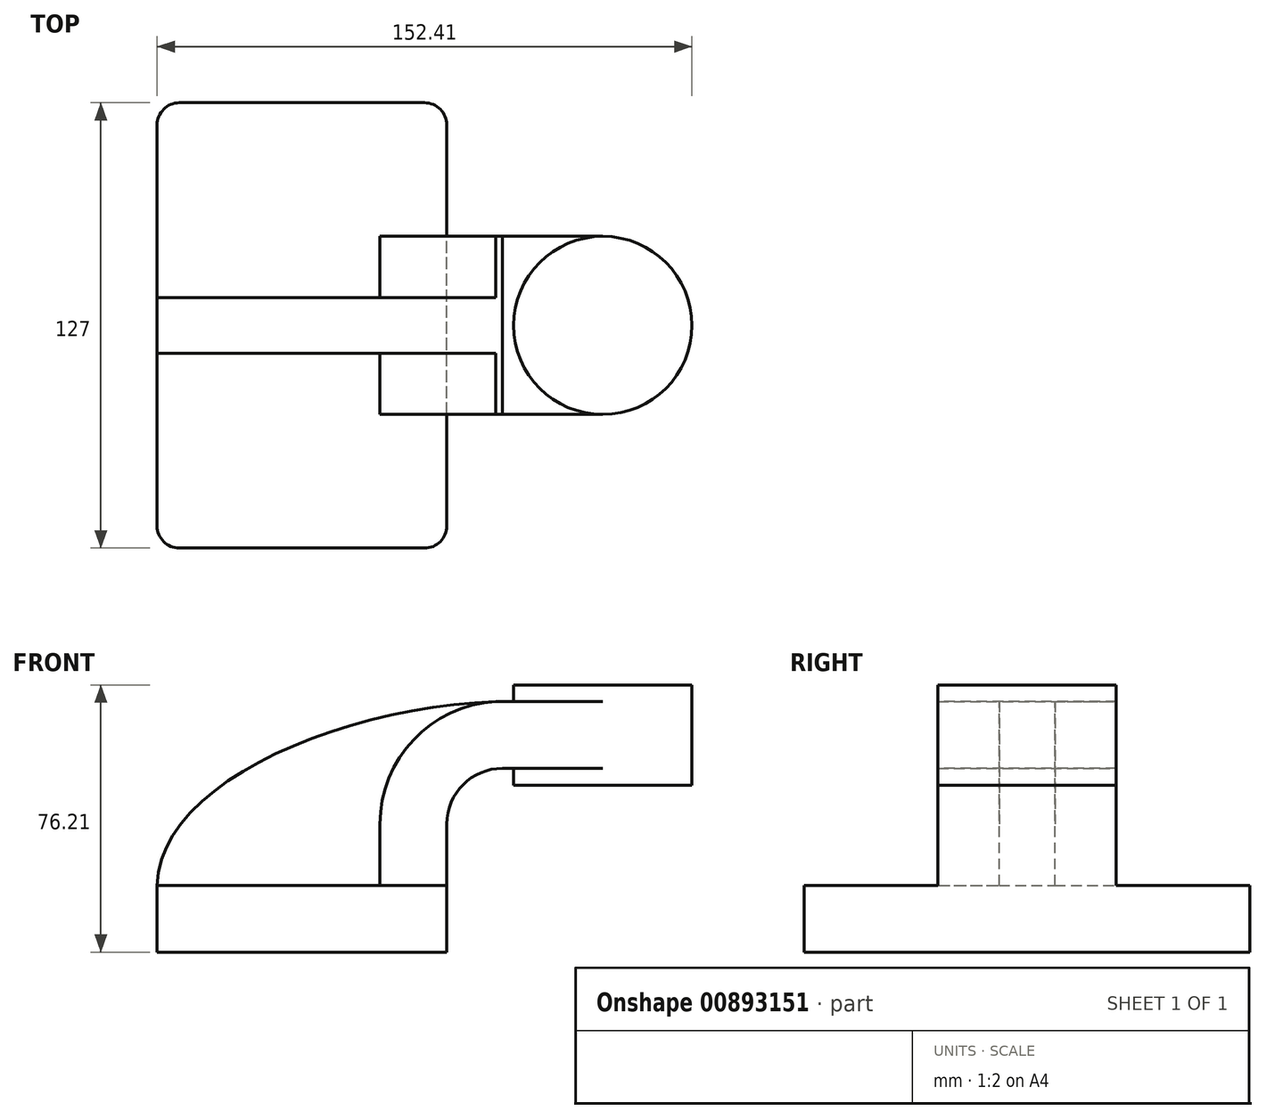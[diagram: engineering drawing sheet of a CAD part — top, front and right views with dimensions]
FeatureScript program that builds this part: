
annotation { "Feature Type Name" : "Feature", "Feature Type Description" : "" }
export const myFeature = defineFeature(function(context is Context, id is Id, definition is map)
    precondition{}
    {
        {
            var Q0;
            Q0=qCreatedBy(makeId("Front.planeOp"),FACE);
            var sketch = newSketch(context, id + "F0", { "sketchPlane" : qUnion([Q0])});
            skLineSegment(sketch, "E0.bottom", {"start": v(-41.28, 9.52) * mm, "end": v(41.27, 9.53) * mm});
            skLineSegment(sketch, "E0.top", {"start": v(-41.28, -9.53) * mm, "end": v(41.28, -9.53) * mm});
            skLineSegment(sketch, "E0.left", {"start": v(-41.28, 9.52) * mm, "end": v(-41.27, -9.53) * mm});
            skLineSegment(sketch, "E0.right", {"start": v(41.28, 9.53) * mm, "end": v(41.28, -9.52) * mm});
            skPoint(sketch, "E0.middle", {"position": v(0, 0) * mm});
            skLineSegment(sketch, "E1.bottom", {"start": v(111.12, 38.1) * mm, "end": v(60.32, 38.1) * mm});
            skLineSegment(sketch, "E1.top", {"start": v(111.12, 66.67) * mm, "end": v(60.32, 66.67) * mm});
            skLineSegment(sketch, "E1.left", {"start": v(111.12, 38.1) * mm, "end": v(111.12, 66.68) * mm});
            skLineSegment(sketch, "E1.right", {"start": v(60.32, 38.1) * mm, "end": v(60.32, 66.67) * mm});
            skPoint(sketch, "E1.middle", {"position": v(85.72, 52.39) * mm});
            skLineSegment(sketch, "E2", {"start": v(41.27, 9.53) * mm, "end": v(41.27, 27) * mm});
            skArc(sketch, "E3", {"start": v(57.15, 42.88) * mm, "mid": v(45.92, 38.23) * mm, "end": v(41.27, 27) * mm});
            skLineSegment(sketch, "E4", {"start": v(57.15, 42.88) * mm, "end": v(85.72, 42.88) * mm});
            skLineSegment(sketch, "E5.0", {"start": v(22.23, 9.53) * mm, "end": v(22.23, 27) * mm});
            skArc(sketch, "E5.1", {"start": v(57.15, 61.93) * mm, "mid": v(32.45, 51.7) * mm, "end": v(22.22, 27) * mm});
            skLineSegment(sketch, "E5.2", {"start": v(57.15, 61.93) * mm, "end": v(85.72, 61.93) * mm});
            skFitSpline(sketch, "E6", {"points": [v(-41.28, 9.52) * mm, v(57.15, 61.93) * mm], "startDerivative": vector(0.89, 86.65) * mm, "endDerivative": vector(137.6, 2.87) * mm});
            skLineSegment(sketch, "E7", {"start": v(85.72, 66.67) * mm, "end": v(85.72, 38.1) * mm});
            skSolve(sketch);
        }
        {
            var Q0;
            Q0=makeQuery(id+"F0.imprint","IMPRINT",FACE,{"disambiguationData":[TD([[makeQuery(id+"F0.imprint","IMPRINT",EDGE,{"derivedFrom":sQuery(id+"F0.wireOp",EDGE,"E0.top")}),1.0]])]});
            extrude(context, id + "F1", {"entities" : qUnion([Q0]), "endBound" : BoundingType.SYMMETRIC, "depth" : 127 * mm, "offsetDistance" : 25.4 * mm});
        }
        {
            var Q0;
            {var subQ1=sQuery(id+"F0.wireOp",EDGE,"E2");Q0=makeQuery(id+"F0.imprint","IMPRINT",FACE,{"disambiguationData":[TD([[makeQuery(id+"F0.imprint","IMPRINT",EDGE,{"derivedFrom":subQ1}),1.0]])]});}
            var Q1;
            {var subQ0=sQuery(id+"F0.wireOp",EDGE,"E4");var subQ1=sQuery(id+"F0.wireOp",EDGE,"E1.right");var subQ2=makeQuery(id+"F0.imprint","INTERSECT",VERTEX,{"derivedFrom":[subQ1,subQ0]});Q1=makeQuery(id+"F0.imprint","IMPRINT",FACE,{"disambiguationData":[TD([[makeQuery(id+"F0.imprint","IMPRINT",EDGE,{"disambiguationData":[TD([[subQ2,-1.0]])],"derivedFrom":subQ1}),-1.0]])]});}
            extrude(context, id + "F2", {"entities" : qUnion([Q0, Q1]), "operationType" : NewBodyOperationType.ADD, "endBound" : BoundingType.SYMMETRIC, "depth" : 50.8 * mm, "offsetDistance" : 25.4 * mm});
        }
        {
            var Q0;
            {var subQ3=sQuery(id+"F0.wireOp",EDGE,"E5.0");Q0=makeQuery(id+"F0.imprint","IMPRINT",FACE,{"disambiguationData":[TD([[makeQuery(id+"F0.imprint","IMPRINT",EDGE,{"derivedFrom":subQ3}),1.0]])]});}
            extrude(context, id + "F3", {"entities" : qUnion([Q0]), "operationType" : NewBodyOperationType.ADD, "endBound" : BoundingType.SYMMETRIC, "depth" : 15.88 * mm, "offsetDistance" : 25.4 * mm});
        }
        {
            var Q0;
            {var subQ4=sQuery(id+"F0.wireOp",EDGE,"E1.left");Q0=makeQuery(id+"F0.imprint","IMPRINT",FACE,{"disambiguationData":[TD([[makeQuery(id+"F0.imprint","IMPRINT",EDGE,{"derivedFrom":subQ4}),1.0]])]});}
            var Q1;
            Q1=sQuery(id+"F0.wireOp",EDGE,"E7");
            revolve(context, id + "F4", {"operationType" : NewBodyOperationType.ADD, "surfaceOperationType" : NewSurfaceOperationType.NEW, "entities" : qUnion([Q0]), "axis" : qUnion([Q1]), "revolveType" : RevolveType.FULL});
        }
        {
            var Q0;
            Q0=makeQuery(id+"F1.opExtrude","CAP_EDGE",EDGE,{"disambiguationData":[OSD([sQuery(id+"F0.wireOp",EDGE,"E0.left")])],"isStart":false});
            var Q1;
            Q1=makeQuery(id+"F1.opExtrude","CAP_EDGE",EDGE,{"disambiguationData":[OSD([sQuery(id+"F0.wireOp",EDGE,"E0.right")])],"isStart":false});
            var Q2;
            Q2=makeQuery(id+"F1.opExtrude","CAP_EDGE",EDGE,{"disambiguationData":[OSD([sQuery(id+"F0.wireOp",EDGE,"E0.right")])],"isStart":true});
            var Q3;
            Q3=makeQuery(id+"F1.opExtrude","CAP_EDGE",EDGE,{"disambiguationData":[OSD([sQuery(id+"F0.wireOp",EDGE,"E0.left")])],"isStart":true});
            fillet(context, id + "F5", {"entities" : qUnion([Q0, Q1, Q2, Q3]), "radius" : 6.35 * mm, "tangentPropagation" : true, "allowEdgeOverflow" : false});
        }
    });
